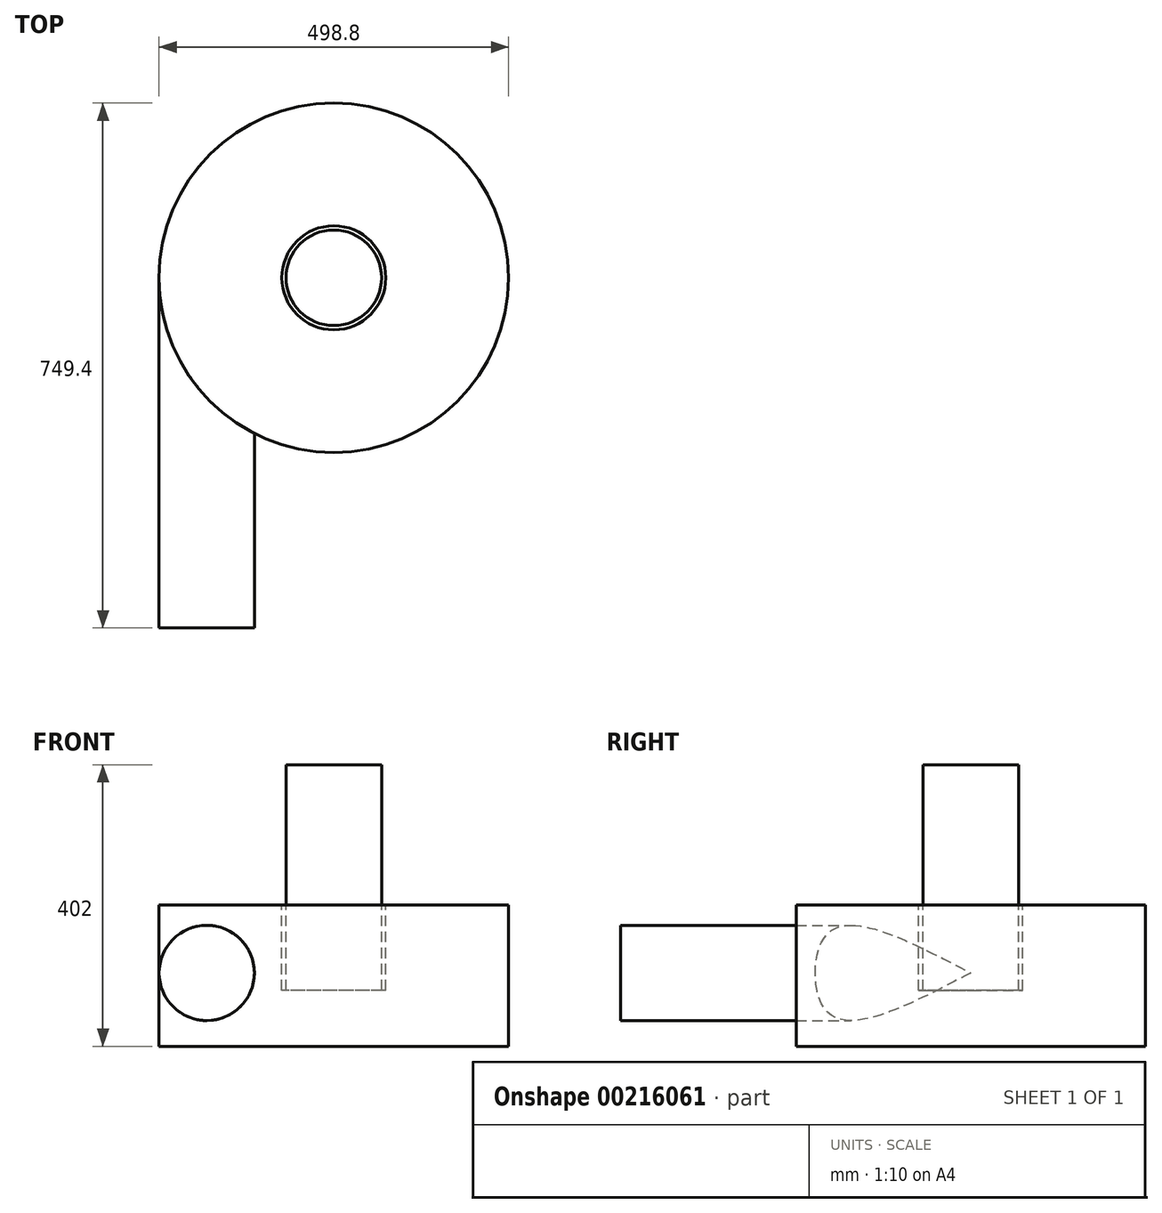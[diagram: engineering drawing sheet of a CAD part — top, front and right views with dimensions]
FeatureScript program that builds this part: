
annotation { "Feature Type Name" : "Feature", "Feature Type Description" : "" }
export const myFeature = defineFeature(function(context is Context, id is Id, definition is map)
    precondition{}
    {
        {
            var Q0;
            Q0=qCreatedBy(makeId("Front.planeOp"),FACE);
            var sketch = newSketch(context, id + "F0", { "sketchPlane" : qUnion([Q0])});
            skLineSegment(sketch, "E0", {"start": v(-114, 165.3) * mm, "end": v(-249.4, 165.3) * mm});
            skLineSegment(sketch, "E1", {"start": v(-249.4, 165.3) * mm, "end": v(-249.4, 367.3) * mm});
            skLineSegment(sketch, "E2", {"start": v(-249.4, 367.3) * mm, "end": v(-74.2, 367.3) * mm});
            skLineSegment(sketch, "E3", {"start": v(-74.2, 367.3) * mm, "end": v(-74.2, 245) * mm});
            skLineSegment(sketch, "E4", {"start": v(-74.2, 245) * mm, "end": v(-68.2, 245) * mm});
            skLineSegment(sketch, "E5", {"start": v(-68.2, 245) * mm, "end": v(-68.2, 367.3) * mm});
            skLineSegment(sketch, "E6", {"start": v(-68.2, 367.3) * mm, "end": v(0, 367.3) * mm});
            skLineSegment(sketch, "E7", {"start": v(0, 367.3) * mm, "end": v(0, 165.3) * mm});
            skLineSegment(sketch, "E8", {"start": v(-114, 165.3) * mm, "end": v(0, 165.3) * mm});
            skSolve(sketch);
        }
        {
            var Q0;
            Q0=makeQuery(id+"F0.imprint","IMPRINT",FACE,{"disambiguationData":[TD([[makeQuery(id+"F0.imprint","IMPRINT",EDGE,{"derivedFrom":sQuery(id+"F0.wireOp",EDGE,"E0")}),-1.0]])]});
            var Q1;
            Q1=sQuery(id+"F0.wireOp",EDGE,"E7");
            revolve(context, id + "F1", {"entities" : qUnion([Q0]), "axis" : qUnion([Q1]), "revolveType" : RevolveType.FULL});
        }
        {
            var Q0;
            Q0=qCreatedBy(makeId("Front.planeOp"),FACE);
            var sketch = newSketch(context, id + "F2", { "sketchPlane" : qUnion([Q0])});
            skCircle(sketch, "E9", {"center": v(-181.4, 270) * mm, "radius": 68 * mm});
            skSolve(sketch);
        }
        {
            var Q0;
            Q0 = qSketchRegion(id + "F2", true);
            extrude(context, id + "F3", {"entities" : qUnion([Q0]), "operationType" : NewBodyOperationType.ADD, "depth" : 500 * mm});
        }
        {
            var Q0;
            Q0=makeQuery(id+"F1.opRevolve","SWEPT_FACE",FACE,{"disambiguationData":[OSD([sQuery(id+"F0.wireOp",EDGE,"E6")])]});
            extrude(context, id + "F4", {"entities" : qUnion([Q0]), "operationType" : NewBodyOperationType.ADD, "depth" : 200 * mm});
        }
    });
